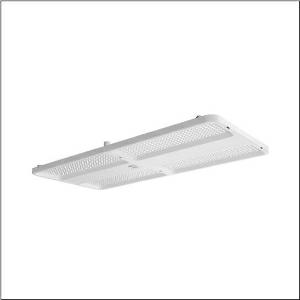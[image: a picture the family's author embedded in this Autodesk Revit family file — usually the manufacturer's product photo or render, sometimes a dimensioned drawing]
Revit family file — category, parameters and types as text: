
# Revit family: highbay_11_maxi_51hn11db4qda03
name_source: partatom
category: Lighting Fixtures
units: mm (PartAtom-declared; Revit-internal decimal feet)

## family parameters
Cut with Voids When Loaded = No
Host = Face
Light Source = No
Part Type = Normal
Room Calculation Point = No
Round Connector Dimension = Use Diameter
Shared = No

## types (1)
- --- (1 x LED, 36000 lm, 177.7 W, 4000K)
    Apparent Load = 178 VA
    CIE Flux Codes = 85 97 100 100 100
    Color Rendering = 80
    Color Temperature = 4000K
    Default Elevation = 1800 mm
    Description = high bay luminaire Highbay 11 maxi; direct symmetric narrow distribution, light control with lens of PMMA; UGR ≤ 22 (X = 4H | Y = 8H | S = 0.25H | reflection values 70/50/20); luminous flux: 36.000lm; light colour: 840, colour temperature: 4000K, MacAdam ≤ 2 SDCM (initial), colour rendering: CRI > 80; luminous efficacy: 202,6lm/W; rated service life: 100.000h (L95/B50) at AT= 25°C; control: DALI 2; for wired networking: open and standardized DALI2 interface enables full flexibility and future-proofing for changes in use or functional adaptation through individual programming; multi-sensor luminaire consisting of a DALI2 multi-sensor and DALI2 ECG; multi-sensor luminaire for wired connection to a DALI2 application controller (e.g., SITECO Connect 11 or 21); can also be connected to existing on-site lighting or building automation systems upon request; integrated DALI2 sensor certified according to IEC 62386, Parts 101, 103, 303, and 304; integrated DALI2 ECG provides luminaire data (according to IEC 62386, Part 251), energy data (Part 252), and monitoring and analytics data (Part 253) to higher-level systems for further processing; luminaire with PIR sensor (passive-infrared); with light sensor; luminaire connection: terminal, 5-pole, max. 2.5mm² (cable entry for one cable, Ø 8.5..16mm); mains connection: 230..240V, AC 50/60Hz; connected load: 177,7W; protection rating (complete): IP65; insulation class (complete): insulation class I (protective earthing); protection symbol: D; certification: CE, ENEC, VDE, UKCA; internal wiring halogen-free; luminaire corresponds to IFS (International Featured Standards) requirements for safety and quality in the food industry; LABS conformity tested according to VDMA 24364:2018-05; housing frame of high-performance plastic PA6, matt traffic white (RAL 9016); cover of PMMA; dimension (LxWxH): 946 x 442 x 72mm; permissible operating ambient temperature: -20..+40°C (reducing of maximum allowable ambient temperature of 5°C with ceiling mounting); packaging unit: 1 piece; (delivery without accessories; please order mounting accessories separately)
    Height = 72 mm  [stored 0.23622 ft]
    Lamp = 1 x LED
    Lamp Light Flux = 36000 lm
    Lamp Power = 177.7 W
    Lamp count = 1
    Length = 946 mm
    Luminous efficacy = 203 lm/W
    Manufacturer = Siteco
    ModVariant = No
    Model = 51HN11DB4QDA03
    Mounting Place = Ceiling
    Mounting Type = Pendant
    Number of Poles = 1
    OnlyDefault = Yes
    Power Factor = 1
    Product Name = Highbay 11 maxi
    Product group = high bay luminaire
    ProductGroupID = 901
    Protection Class = Protection class I
    Protection Degree = IP 65
    RLX_Detail_Level = 1
    RLX_Emergency_Light_Flux = 0 lm
    RLX_Emergency_Type = 0
    RLX_Emergency_Type_DB = No
    RlxData = <blob elided: 127305 chars, md5=7d0f9877>
    Socket = socket
    Standby Power = 0 W
    System Light Flux = 36000 lm
    System Power = 178 W
    Type Comments = factory setting: luminous flux: 100 % | dim-lin: 254 | 824 mA
    Type Image = l_1363267.jpg
    URL = http://relux.com
    VarID = @adj_022419
    Voltage = 0 V
    Weight = 0.00 kg
    Width = 442 mm

note: [stored X ft] marks values corroborated as IEEE doubles in the binary element streams (Revit-internal decimal feet)

## geometry (parser evidence)
native form markers: Blend x4, Sweep x11
no freeform markers — native parametric forms only
